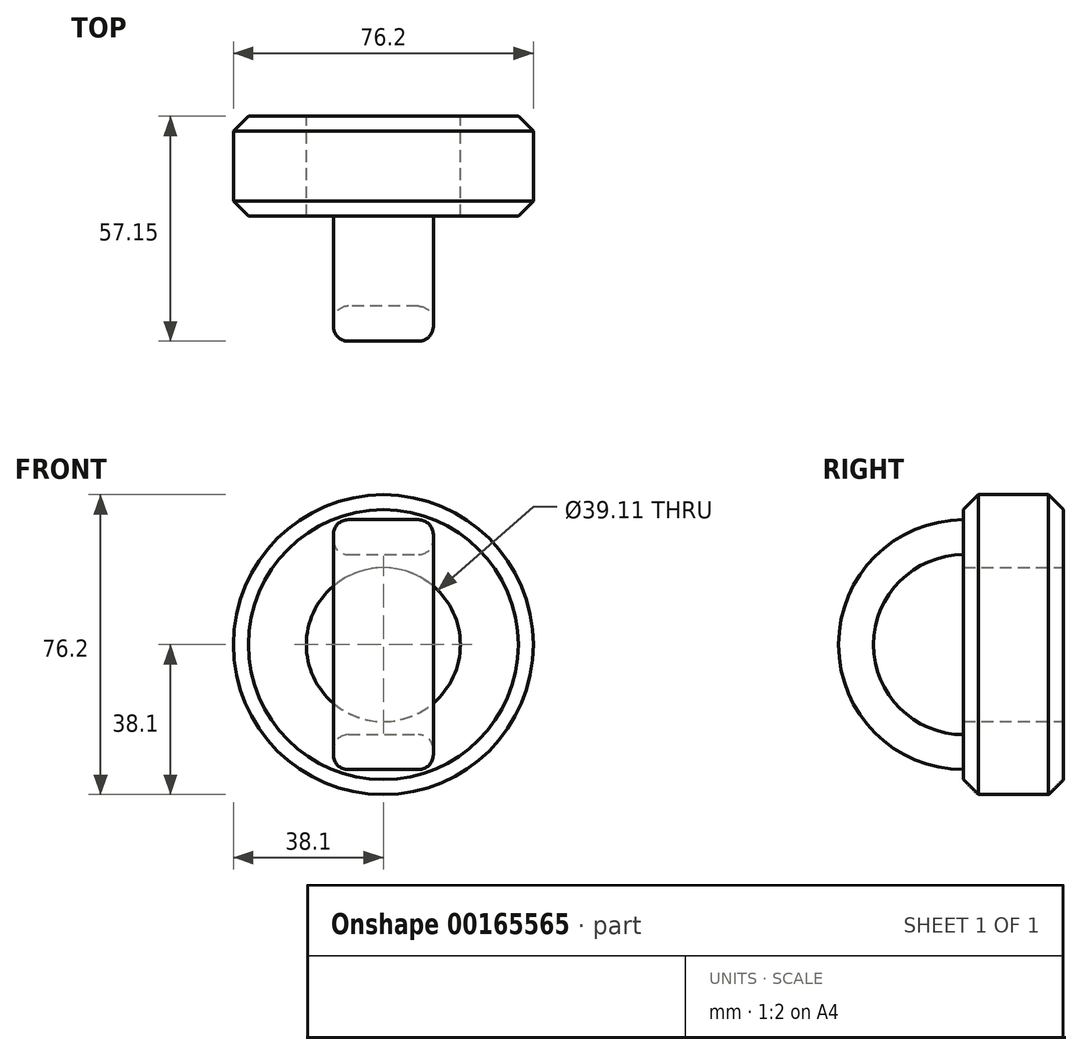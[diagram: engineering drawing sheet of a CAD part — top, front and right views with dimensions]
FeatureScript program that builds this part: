
annotation { "Feature Type Name" : "Feature", "Feature Type Description" : "" }
export const myFeature = defineFeature(function(context is Context, id is Id, definition is map)
    precondition{}
    {
        {
            var Q0;
            Q0=qCreatedBy(makeId("Front.planeOp"),FACE);
            var sketch = newSketch(context, id + "F0", { "sketchPlane" : qUnion([Q0])});
            skCircle(sketch, "E0", {"center": v(0, 0) * mm, "radius": 38.1 * mm});
            skCircle(sketch, "E1", {"center": v(0, 0) * mm, "radius": 19.56 * mm});
            skSolve(sketch);
        }
        {
            var Q0;
            Q0 = qSketchRegion(id + "F0", true);
            extrude(context, id + "F1", {"entities" : qUnion([Q0]), "depth" : 25.4 * mm});
        }
        {
            var Q0;
            Q0=makeQuery(id+"F1.opExtrude","CAP_FACE",FACE,{"disambiguationData":[OSD([sQuery(id+"F0.wireOp",EDGE,"E0"),sQuery(id+"F0.wireOp",EDGE,"E1")])],"isStart":false});
            var sketch = newSketch(context, id + "F2", { "sketchPlane" : qUnion([Q0])});
            skLineSegment(sketch, "E2", {"start": v(-12.7, 22.86) * mm, "end": v(12.7, 22.86) * mm});
            skLineSegment(sketch, "E3", {"start": v(-12.7, 22.86) * mm, "end": v(-12.7, 31.75) * mm});
            skLineSegment(sketch, "E4", {"start": v(12.7, 22.86) * mm, "end": v(12.7, 31.75) * mm});
            skLineSegment(sketch, "E5", {"start": v(-12.7, 31.75) * mm, "end": v(12.7, 31.75) * mm});
            skLineSegment(sketch, "E6", {"start": v(-48.5, 0) * mm, "end": v(67.2, 0) * mm});
            skSolve(sketch);
        }
        {
            var Q0;
            Q0=makeQuery(id+"F2.imprint","IMPRINT",FACE,{"disambiguationData":[TD([[makeQuery(id+"F2.imprint","IMPRINT",EDGE,{"derivedFrom":sQuery(id+"F2.wireOp",EDGE,"E2")}),1.0]])]});
            var Q1;
            Q1=sQuery(id+"F2.wireOp",EDGE,"E6");
            revolve(context, id + "F3", {"operationType" : NewBodyOperationType.ADD, "entities" : qUnion([Q0]), "axis" : qUnion([Q1]), "revolveType" : RevolveType.ONE_DIRECTION, "angle" : 180 * degree});
        }
        {
            var Q0;
            Q0=makeQuery(id+"F3.opRevolve","SWEPT_EDGE",EDGE,{"disambiguationData":[OSD([sQuery(id+"F2.wireOp",EDGE,"E3"),sQuery(id+"F2.wireOp",EDGE,"E5")])]});
            var Q1;
            Q1=makeQuery(id+"F3.opRevolve","SWEPT_EDGE",EDGE,{"disambiguationData":[OSD([sQuery(id+"F2.wireOp",EDGE,"E4"),sQuery(id+"F2.wireOp",EDGE,"E5")])]});
            var Q2;
            Q2=makeQuery(id+"F3.opRevolve","SWEPT_EDGE",EDGE,{"disambiguationData":[OSD([sQuery(id+"F2.wireOp",EDGE,"E2"),sQuery(id+"F2.wireOp",EDGE,"E4")])]});
            var Q3;
            Q3=makeQuery(id+"F3.opRevolve","SWEPT_EDGE",EDGE,{"disambiguationData":[OSD([sQuery(id+"F2.wireOp",EDGE,"E2"),sQuery(id+"F2.wireOp",EDGE,"E3")])]});
            fillet(context, id + "F4", {"entities" : qUnion([Q0, Q1, Q2, Q3]), "radius" : 3.8 * mm, "tangentPropagation" : true, "allowEdgeOverflow" : false});
        }
        {
            var Q0;
            Q0=makeQuery(id+"F1.opExtrude","SWEPT_FACE",FACE,{"disambiguationData":[OSD([sQuery(id+"F0.wireOp",EDGE,"E0")])]});
            chamfer(context, id + "F5", {"entities" : qUnion([Q0]), "width" : 3.8 * mm, "tangentPropagation" : true});
        }
    });
